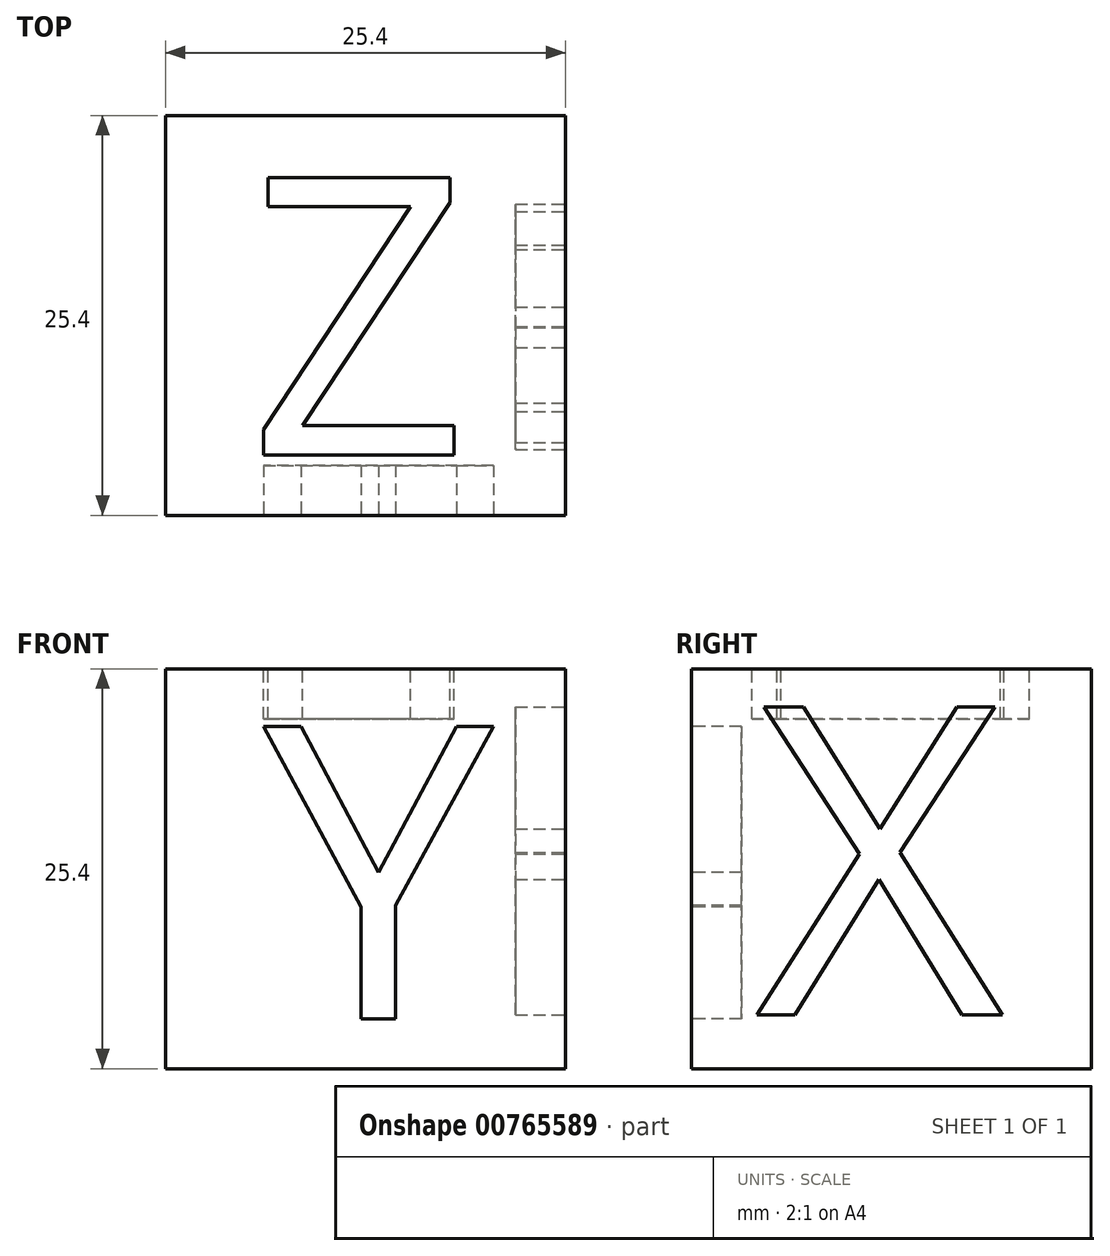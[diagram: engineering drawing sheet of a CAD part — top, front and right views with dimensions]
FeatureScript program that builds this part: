
annotation { "Feature Type Name" : "Feature", "Feature Type Description" : "" }
export const myFeature = defineFeature(function(context is Context, id is Id, definition is map)
    precondition{}
    {
        {
            var Q0;
            Q0=qCreatedBy(makeId("Top.planeOp"),FACE);
            var sketch = newSketch(context, id + "F0", { "sketchPlane" : qUnion([Q0])});
            skLineSegment(sketch, "E0.bottom", {"start": v(12.7, -12.7) * mm, "end": v(-12.7, -12.7) * mm});
            skLineSegment(sketch, "E0.top", {"start": v(12.7, 12.7) * mm, "end": v(-12.7, 12.7) * mm});
            skLineSegment(sketch, "E0.left", {"start": v(12.7, -12.7) * mm, "end": v(12.7, 12.7) * mm});
            skLineSegment(sketch, "E0.right", {"start": v(-12.7, -12.7) * mm, "end": v(-12.7, 12.7) * mm});
            skPoint(sketch, "E0.middle", {"position": v(0, 0) * mm});
            skSolve(sketch);
        }
        {
            var Q0;
            Q0 = qSketchRegion(id + "F0", true);
            extrude(context, id + "F1", {"entities" : qUnion([Q0]), "depth" : 25.4 * mm, "offsetDistance" : 25.4 * mm});
        }
        {
            var Q0;
            Q0=makeQuery(id+"F1.opExtrude","CAP_FACE",FACE,{"disambiguationData":[OSD([sQuery(id+"F0.wireOp",EDGE,"E0.bottom"),sQuery(id+"F0.wireOp",EDGE,"E0.top"),sQuery(id+"F0.wireOp",EDGE,"E0.left"),sQuery(id+"F0.wireOp",EDGE,"E0.right")])],"isStart":false});
            var sketch = newSketch(context, id + "F2", { "sketchPlane" : qUnion([Q0])});
            skText(sketch, "E1", { "text": "Z", "fontName": "OpenSans-Regular.ttf"});
            const initialGuessF2  = {"E1": [-0.00748, -0.00887, 1, 0, 0.01778]};
            skSetInitialGuess(sketch, initialGuessF2);
            skSolve(sketch);
        }
        {
            var Q0;
            Q0=makeQuery(id+"F2.imprint","IMPRINT",FACE,{"disambiguationData":[TD([[makeQuery(id+"F2.imprint","IMPRINT",EDGE,{"derivedFrom":sQuery(id+"F2.wireOp",EDGE,"E1.sketch_text.stroke-0")}),-1.0]])]});
            extrude(context, id + "F3", {"entities" : qUnion([Q0]), "operationType" : NewBodyOperationType.REMOVE, "oppositeDirection" : true, "depth" : 3.17 * mm, "offsetDistance" : 25.4 * mm});
        }
        {
            var Q0;
            Q0=makeQuery(id+"F1.opExtrude","SWEPT_FACE",FACE,{"disambiguationData":[OSD([sQuery(id+"F0.wireOp",EDGE,"E0.bottom")])]});
            var sketch = newSketch(context, id + "F4", { "sketchPlane" : qUnion([Q0])});
            skText(sketch, "E2", { "text": "Y", "fontName": "OpenSans-Regular.ttf"});
            const initialGuessF4  = {"E2": [-0.00647, 0.00316, 1, 0, 0.01875]};
            skSetInitialGuess(sketch, initialGuessF4);
            skSolve(sketch);
        }
        {
            var Q0;
            Q0 = qSketchRegion(id + "F4", true);
            extrude(context, id + "F5", {"entities" : qUnion([Q0]), "operationType" : NewBodyOperationType.REMOVE, "oppositeDirection" : true, "depth" : 3.17 * mm, "offsetDistance" : 25.4 * mm});
        }
        {
            var Q0;
            Q0=makeQuery(id+"F1.opExtrude","SWEPT_FACE",FACE,{"disambiguationData":[OSD([sQuery(id+"F0.wireOp",EDGE,"E0.left")])]});
            var sketch = newSketch(context, id + "F6", { "sketchPlane" : qUnion([Q0])});
            skText(sketch, "E3", { "text": "X", "fontName": "OpenSans-Regular.ttf"});
            const initialGuessF6  = {"E3": [-0.00864, 0.00343, 1, 0, 0.01971]};
            skSetInitialGuess(sketch, initialGuessF6);
            skSolve(sketch);
        }
        {
            var Q0;
            Q0 = qSketchRegion(id + "F6", true);
            extrude(context, id + "F7", {"entities" : qUnion([Q0]), "operationType" : NewBodyOperationType.REMOVE, "oppositeDirection" : true, "depth" : 3.17 * mm, "offsetDistance" : 25.4 * mm});
        }
    });
